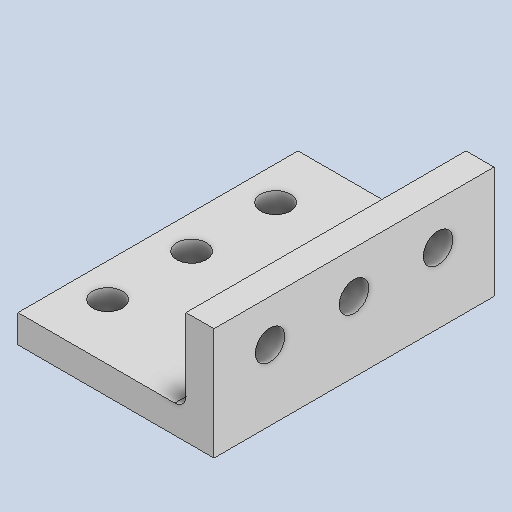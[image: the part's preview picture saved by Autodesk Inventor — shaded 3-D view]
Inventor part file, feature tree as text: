
AUTODESK INVENTOR PART (.ipt)
format: ipt  version: 2022 (Build 260153000, 153)  size: 125,952 bytes
history: native  units: in
note: dims shown in document units (in); Inventor stores cm internally (conversion verified against a paired STEP export)
features: other x3, sketch x3
ambient origin geometry x8: Origin, YZ Plane, XZ Plane, XY Plane, X Axis, Y Axis, Z Axis, Center Point
bodies: Solid1 (feature_tree)
feature tree (6):
  other  "Linear Rail Frame Bracket.ipt"
  other  "Solid1::Linear Rail Frame Bracket.ipt"
  other  "TaggingFeature1"
  sketch  "Sketch1"  dims[d0=0.3937in]
  sketch  "Sketch2"
  sketch  "Sketch3"
